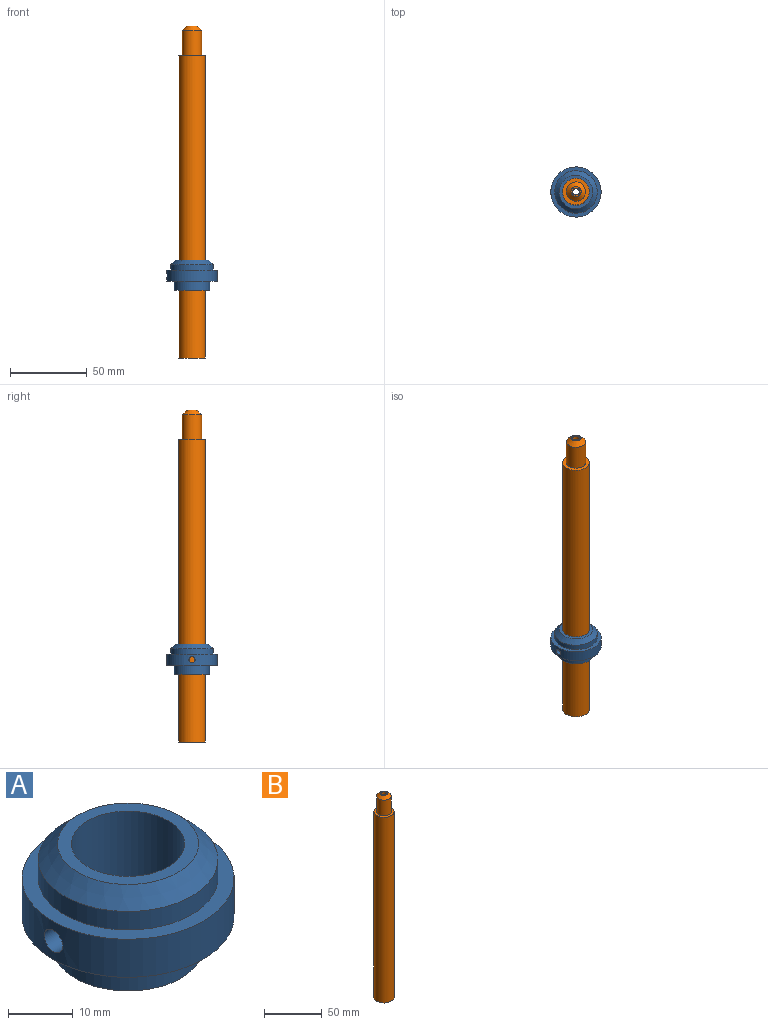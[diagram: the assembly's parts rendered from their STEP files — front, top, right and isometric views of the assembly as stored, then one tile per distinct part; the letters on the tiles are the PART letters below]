
ASSEMBLY  parts=2 mates=1
PART A: 10 faces, bbox 32.8x32.8x19.7 mm
  f0: cylinder r=16.4mm len=32.8mm, axis (0,0,-1), area 729.4mm2, adj f5,f7,f9
  f1: plane 21.8x21.8mm, normal (0,0,1), area 132.7mm2, adj f2,f8
  f2: cylinder r=8.75mm len=19.7mm, axis (0,0,-1), area 1070.5mm2, adj f1,f3,f9
  f3: plane 23.1x23.1mm, normal (0,0,-1), area 178.6mm2, adj f2,f4
  f4: cylinder r=11.55mm len=23.1mm, axis (0,0,-1), area 435.4mm2, adj f3,f5
  f5: plane 32.8x32.8mm, normal (0,0,-1), area 425.9mm2, adj f0,f4
  f6: cylinder r=13.9mm len=27.8mm, axis (0,0,1), area 305.7mm2, adj f7,f8
  f7: plane 32.8x32.8mm, normal (0,0,1), area 238mm2, adj f0,f6
  f8: cone r=10.9mm half-angle=45deg, axis (0,0,-1), area 330.6mm2, adj f1,f6
  f9: cylinder r=2mm len=7.88mm, axis (1,0,0), area 96.8mm2, adj f0,f2
PART B: 7 faces, bbox 17.5x17.5x217 mm
  f0: cylinder r=8.75mm len=197.4mm, axis (0,0,1), area 10852.6mm2, adj f3,f5
  f1: plane 6.6x6.6mm, normal (0,0,1), area 18.3mm2, adj f2,f6
  f2: cylinder r=2.25mm len=217mm, axis (0,0,1), area 3067.8mm2, adj f1,f3
  f3: plane 17.5x17.5mm, normal (0,0,-1), area 224.6mm2, adj f0,f2
  f4: cylinder r=6.3mm len=16.6mm, axis (0,0,1), area 657.1mm2, adj f5,f6
  f5: plane 17.5x17.5mm, normal (0,0,1), area 115.8mm2, adj f0,f4
  f6: cone r=3.3mm half-angle=45deg, axis (0,0,-1), area 128mm2, adj f1,f4
PLACE A t=(6.84,-19.69,-117.38)mm
PLACE B t=(6.84,-19.69,55.32)mm
MATE fastened A.f2 <-> B.f2  axis (0,0,1) through (6.84,-19.69,-97.68)mm
